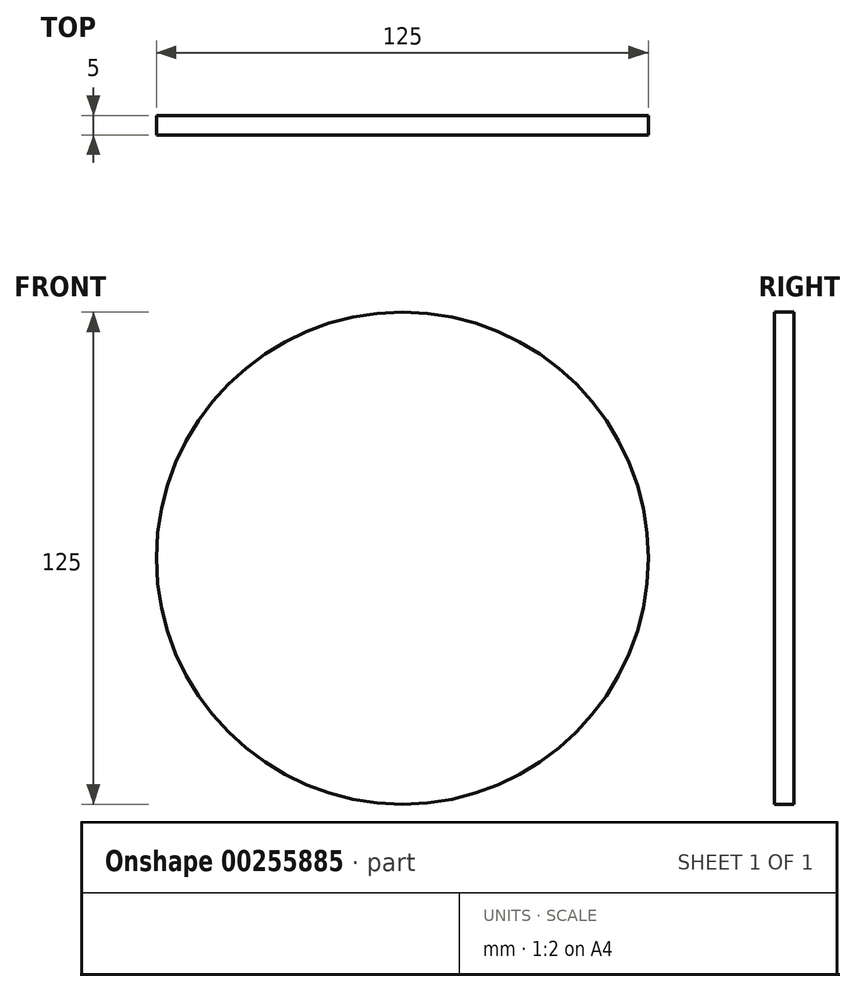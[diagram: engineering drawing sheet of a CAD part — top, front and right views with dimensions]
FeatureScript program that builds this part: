
annotation { "Feature Type Name" : "Feature", "Feature Type Description" : "" }
export const myFeature = defineFeature(function(context is Context, id is Id, definition is map)
    precondition{}
    {
        {
            var Q0;
            Q0=qCreatedBy(makeId("Front.planeOp"),FACE);
            var sketch = newSketch(context, id + "F0", { "sketchPlane" : qUnion([Q0])});
            skCircle(sketch, "E0", {"center": v(-16.9, 22.06) * mm, "radius": 62.5 * mm});
            skSolve(sketch);
        }
        {
            var Q0;
            Q0 = qSketchRegion(id + "F0", true);
            var Q1;
            Q1=makeQuery(id+"F0.imprint","IMPRINT",FACE,{"disambiguationData":[TD([[makeQuery(id+"F0.imprint","IMPRINT",EDGE,{"derivedFrom":sQuery(id+"F0.wireOp",EDGE,"E0")}),1.0]])]});
            extrude(context, id + "F1", {"entities" : qUnion([Q0, Q1]), "depth" : 5 * mm});
        }
    });
